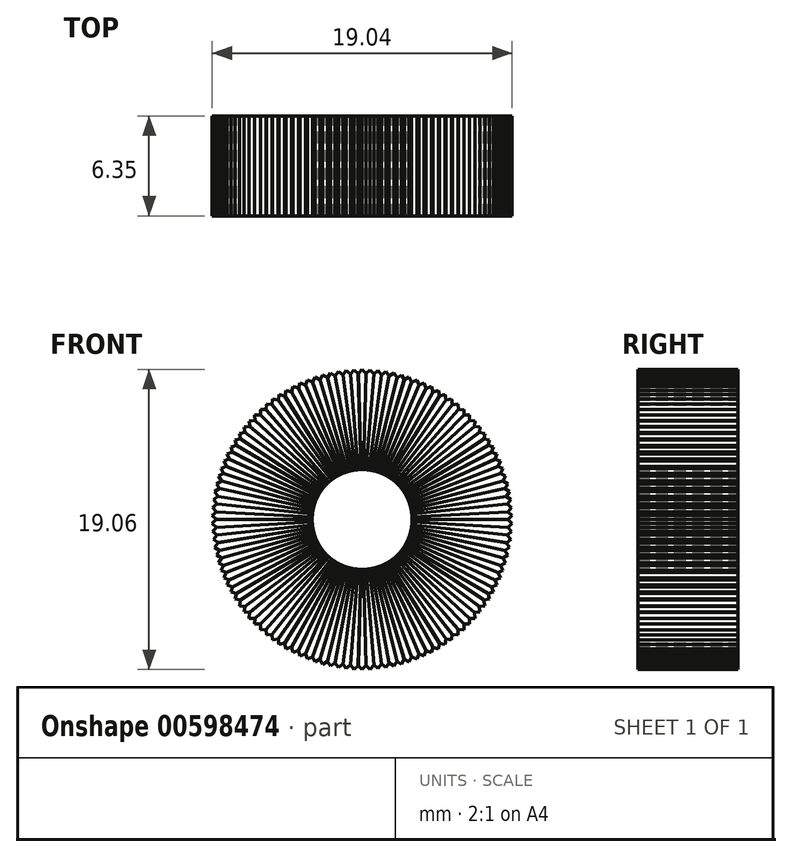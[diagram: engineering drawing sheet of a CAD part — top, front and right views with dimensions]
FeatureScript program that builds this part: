
annotation { "Feature Type Name" : "Feature", "Feature Type Description" : "" }
export const myFeature = defineFeature(function(context is Context, id is Id, definition is map)
    precondition{}
    {
        {
            var Q0;
            Q0=qCreatedBy(makeId("Front.planeOp"),FACE);
            var sketch = newSketch(context, id + "F0", { "sketchPlane" : qUnion([Q0])});
            skCircle(sketch, "E0", {"center": v(0, 0) * mm, "radius": 9.53 * mm});
            skCircle(sketch, "E1", {"center": v(0, 0) * mm, "radius": 3.18 * mm});
            skLineSegment(sketch, "E2", {"start": v(0, 0) * mm, "end": v(0, 9.53) * mm, "construction": true});
            skLineSegment(sketch, "E3.1.0", {"start": v(0, 0) * mm, "end": v(0.25, 9.52) * mm, "construction": true});
            skLineSegment(sketch, "E3.2.0", {"start": v(0, 0) * mm, "end": v(0.5, 9.51) * mm, "construction": true});
            skLineSegment(sketch, "E3.3.0", {"start": v(0, 0) * mm, "end": v(0.76, 9.5) * mm, "construction": true});
            skLineSegment(sketch, "E3.4.0", {"start": v(0, 0) * mm, "end": v(1.01, 9.47) * mm, "construction": true});
            skLineSegment(sketch, "E3.5.0", {"start": v(0, 0) * mm, "end": v(1.26, 9.44) * mm, "construction": true});
            skLineSegment(sketch, "E3.6.0", {"start": v(0, 0) * mm, "end": v(1.52, 9.4) * mm, "construction": true});
            skLineSegment(sketch, "E3.7.0", {"start": v(0, 0) * mm, "end": v(1.76, 9.36) * mm, "construction": true});
            skLineSegment(sketch, "E3.8.0", {"start": v(0, 0) * mm, "end": v(2.01, 9.3) * mm, "construction": true});
            skLineSegment(sketch, "E3.9.0", {"start": v(0, 0) * mm, "end": v(2.26, 9.25) * mm, "construction": true});
            skLineSegment(sketch, "E3.10.0", {"start": v(0, 0) * mm, "end": v(2.5, 9.19) * mm, "construction": true});
            skLineSegment(sketch, "E3.11.0", {"start": v(0, 0) * mm, "end": v(2.75, 9.12) * mm, "construction": true});
            skLineSegment(sketch, "E3.12.0", {"start": v(0, 0) * mm, "end": v(3, 9.04) * mm, "construction": true});
            skLineSegment(sketch, "E3.13.0", {"start": v(0, 0) * mm, "end": v(3.23, 8.96) * mm, "construction": true});
            skLineSegment(sketch, "E3.14.0", {"start": v(0, 0) * mm, "end": v(3.47, 8.87) * mm, "construction": true});
            skLineSegment(sketch, "E3.15.0", {"start": v(0, 0) * mm, "end": v(3.7, 8.78) * mm, "construction": true});
            skLineSegment(sketch, "E3.16.0", {"start": v(0, 0) * mm, "end": v(3.94, 8.67) * mm, "construction": true});
            skLineSegment(sketch, "E3.17.0", {"start": v(0, 0) * mm, "end": v(4.17, 8.57) * mm, "construction": true});
            skLineSegment(sketch, "E3.18.0", {"start": v(0, 0) * mm, "end": v(4.4, 8.45) * mm, "construction": true});
            skLineSegment(sketch, "E3.19.0", {"start": v(0, 0) * mm, "end": v(4.62, 8.33) * mm, "construction": true});
            skLineSegment(sketch, "E3.20.0", {"start": v(0, 0) * mm, "end": v(4.84, 8.2) * mm, "construction": true});
            skLineSegment(sketch, "E3.21.0", {"start": v(0, 0) * mm, "end": v(5.05, 8.07) * mm, "construction": true});
            skLineSegment(sketch, "E3.22.0", {"start": v(0, 0) * mm, "end": v(5.27, 7.94) * mm, "construction": true});
            skLineSegment(sketch, "E3.23.0", {"start": v(0, 0) * mm, "end": v(5.47, 7.8) * mm, "construction": true});
            skLineSegment(sketch, "E3.24.0", {"start": v(0, 0) * mm, "end": v(5.68, 7.65) * mm, "construction": true});
            skLineSegment(sketch, "E3.25.0", {"start": v(0, 0) * mm, "end": v(5.88, 7.5) * mm, "construction": true});
            skLineSegment(sketch, "E3.26.0", {"start": v(0, 0) * mm, "end": v(6.08, 7.33) * mm, "construction": true});
            skLineSegment(sketch, "E3.27.0", {"start": v(0, 0) * mm, "end": v(6.27, 7.17) * mm, "construction": true});
            skLineSegment(sketch, "E3.28.0", {"start": v(0, 0) * mm, "end": v(6.46, 7) * mm, "construction": true});
            skLineSegment(sketch, "E3.29.0", {"start": v(0, 0) * mm, "end": v(6.64, 6.82) * mm, "construction": true});
            skLineSegment(sketch, "E3.30.0", {"start": v(0, 0) * mm, "end": v(6.82, 6.64) * mm, "construction": true});
            skLineSegment(sketch, "E3.31.0", {"start": v(0, 0) * mm, "end": v(7, 6.46) * mm, "construction": true});
            skLineSegment(sketch, "E3.32.0", {"start": v(0, 0) * mm, "end": v(7.17, 6.27) * mm, "construction": true});
            skLineSegment(sketch, "E3.33.0", {"start": v(0, 0) * mm, "end": v(7.33, 6.08) * mm, "construction": true});
            skLineSegment(sketch, "E3.34.0", {"start": v(0, 0) * mm, "end": v(7.5, 5.88) * mm, "construction": true});
            skLineSegment(sketch, "E3.35.0", {"start": v(0, 0) * mm, "end": v(7.65, 5.68) * mm, "construction": true});
            skLineSegment(sketch, "E3.36.0", {"start": v(0, 0) * mm, "end": v(7.8, 5.47) * mm, "construction": true});
            skLineSegment(sketch, "E3.37.0", {"start": v(0, 0) * mm, "end": v(7.94, 5.27) * mm, "construction": true});
            skLineSegment(sketch, "E3.38.0", {"start": v(0, 0) * mm, "end": v(8.07, 5.05) * mm, "construction": true});
            skLineSegment(sketch, "E3.39.0", {"start": v(0, 0) * mm, "end": v(8.2, 4.84) * mm, "construction": true});
            skLineSegment(sketch, "E3.40.0", {"start": v(0, 0) * mm, "end": v(8.33, 4.62) * mm, "construction": true});
            skLineSegment(sketch, "E3.41.0", {"start": v(0, 0) * mm, "end": v(8.45, 4.4) * mm, "construction": true});
            skLineSegment(sketch, "E3.42.0", {"start": v(0, 0) * mm, "end": v(8.57, 4.17) * mm, "construction": true});
            skLineSegment(sketch, "E3.43.0", {"start": v(0, 0) * mm, "end": v(8.67, 3.94) * mm, "construction": true});
            skLineSegment(sketch, "E3.44.0", {"start": v(0, 0) * mm, "end": v(8.78, 3.7) * mm, "construction": true});
            skLineSegment(sketch, "E3.45.0", {"start": v(0, 0) * mm, "end": v(8.87, 3.47) * mm, "construction": true});
            skLineSegment(sketch, "E3.46.0", {"start": v(0, 0) * mm, "end": v(8.96, 3.23) * mm, "construction": true});
            skLineSegment(sketch, "E3.47.0", {"start": v(0, 0) * mm, "end": v(9.04, 3) * mm, "construction": true});
            skLineSegment(sketch, "E3.48.0", {"start": v(0, 0) * mm, "end": v(9.12, 2.75) * mm, "construction": true});
            skLineSegment(sketch, "E3.49.0", {"start": v(0, 0) * mm, "end": v(9.19, 2.5) * mm, "construction": true});
            skLineSegment(sketch, "E3.50.0", {"start": v(0, 0) * mm, "end": v(9.25, 2.26) * mm, "construction": true});
            skLineSegment(sketch, "E3.51.0", {"start": v(0, 0) * mm, "end": v(9.3, 2.01) * mm, "construction": true});
            skLineSegment(sketch, "E3.52.0", {"start": v(0, 0) * mm, "end": v(9.36, 1.76) * mm, "construction": true});
            skLineSegment(sketch, "E3.53.0", {"start": v(0, 0) * mm, "end": v(9.4, 1.52) * mm, "construction": true});
            skLineSegment(sketch, "E3.54.0", {"start": v(0, 0) * mm, "end": v(9.44, 1.26) * mm, "construction": true});
            skLineSegment(sketch, "E3.55.0", {"start": v(0, 0) * mm, "end": v(9.47, 1.01) * mm, "construction": true});
            skLineSegment(sketch, "E3.56.0", {"start": v(0, 0) * mm, "end": v(9.5, 0.76) * mm, "construction": true});
            skLineSegment(sketch, "E3.57.0", {"start": v(0, 0) * mm, "end": v(9.51, 0.5) * mm, "construction": true});
            skLineSegment(sketch, "E3.58.0", {"start": v(0, 0) * mm, "end": v(9.52, 0.25) * mm, "construction": true});
            skLineSegment(sketch, "E3.59.0", {"start": v(0, 0) * mm, "end": v(9.53, 0) * mm, "construction": true});
            skLineSegment(sketch, "E3.60.0", {"start": v(0, 0) * mm, "end": v(9.52, -0.25) * mm, "construction": true});
            skLineSegment(sketch, "E3.61.0", {"start": v(0, 0) * mm, "end": v(9.51, -0.5) * mm, "construction": true});
            skLineSegment(sketch, "E3.62.0", {"start": v(0, 0) * mm, "end": v(9.5, -0.76) * mm, "construction": true});
            skLineSegment(sketch, "E3.63.0", {"start": v(0, 0) * mm, "end": v(9.47, -1.01) * mm, "construction": true});
            skLineSegment(sketch, "E3.64.0", {"start": v(0, 0) * mm, "end": v(9.44, -1.26) * mm, "construction": true});
            skLineSegment(sketch, "E3.65.0", {"start": v(0, 0) * mm, "end": v(9.4, -1.52) * mm, "construction": true});
            skLineSegment(sketch, "E3.66.0", {"start": v(0, 0) * mm, "end": v(9.36, -1.76) * mm, "construction": true});
            skLineSegment(sketch, "E3.67.0", {"start": v(0, 0) * mm, "end": v(9.3, -2.01) * mm, "construction": true});
            skLineSegment(sketch, "E3.68.0", {"start": v(0, 0) * mm, "end": v(9.25, -2.26) * mm, "construction": true});
            skLineSegment(sketch, "E3.69.0", {"start": v(0, 0) * mm, "end": v(9.19, -2.5) * mm, "construction": true});
            skLineSegment(sketch, "E3.70.0", {"start": v(0, 0) * mm, "end": v(9.12, -2.75) * mm, "construction": true});
            skLineSegment(sketch, "E3.71.0", {"start": v(0, 0) * mm, "end": v(9.04, -3) * mm, "construction": true});
            skLineSegment(sketch, "E3.72.0", {"start": v(0, 0) * mm, "end": v(8.96, -3.23) * mm, "construction": true});
            skLineSegment(sketch, "E3.73.0", {"start": v(0, 0) * mm, "end": v(8.87, -3.47) * mm, "construction": true});
            skLineSegment(sketch, "E3.74.0", {"start": v(0, 0) * mm, "end": v(8.78, -3.7) * mm, "construction": true});
            skLineSegment(sketch, "E3.75.0", {"start": v(0, 0) * mm, "end": v(8.67, -3.94) * mm, "construction": true});
            skLineSegment(sketch, "E3.76.0", {"start": v(0, 0) * mm, "end": v(8.57, -4.17) * mm, "construction": true});
            skLineSegment(sketch, "E3.77.0", {"start": v(0, 0) * mm, "end": v(8.45, -4.4) * mm, "construction": true});
            skLineSegment(sketch, "E3.78.0", {"start": v(0, 0) * mm, "end": v(8.33, -4.62) * mm, "construction": true});
            skLineSegment(sketch, "E3.79.0", {"start": v(0, 0) * mm, "end": v(8.2, -4.84) * mm, "construction": true});
            skLineSegment(sketch, "E3.80.0", {"start": v(0, 0) * mm, "end": v(8.07, -5.05) * mm, "construction": true});
            skLineSegment(sketch, "E3.81.0", {"start": v(0, 0) * mm, "end": v(7.94, -5.27) * mm, "construction": true});
            skLineSegment(sketch, "E3.82.0", {"start": v(0, 0) * mm, "end": v(7.8, -5.47) * mm, "construction": true});
            skLineSegment(sketch, "E3.83.0", {"start": v(0, 0) * mm, "end": v(7.65, -5.68) * mm, "construction": true});
            skLineSegment(sketch, "E3.84.0", {"start": v(0, 0) * mm, "end": v(7.5, -5.88) * mm, "construction": true});
            skLineSegment(sketch, "E3.85.0", {"start": v(0, 0) * mm, "end": v(7.33, -6.08) * mm, "construction": true});
            skLineSegment(sketch, "E3.86.0", {"start": v(0, 0) * mm, "end": v(7.17, -6.27) * mm, "construction": true});
            skLineSegment(sketch, "E3.87.0", {"start": v(0, 0) * mm, "end": v(7, -6.46) * mm, "construction": true});
            skLineSegment(sketch, "E3.88.0", {"start": v(0, 0) * mm, "end": v(6.82, -6.64) * mm, "construction": true});
            skLineSegment(sketch, "E3.89.0", {"start": v(0, 0) * mm, "end": v(6.64, -6.82) * mm, "construction": true});
            skLineSegment(sketch, "E3.90.0", {"start": v(0, 0) * mm, "end": v(6.46, -7) * mm, "construction": true});
            skLineSegment(sketch, "E3.91.0", {"start": v(0, 0) * mm, "end": v(6.27, -7.17) * mm, "construction": true});
            skLineSegment(sketch, "E3.92.0", {"start": v(0, 0) * mm, "end": v(6.08, -7.33) * mm, "construction": true});
            skLineSegment(sketch, "E3.93.0", {"start": v(0, 0) * mm, "end": v(5.88, -7.5) * mm, "construction": true});
            skLineSegment(sketch, "E3.94.0", {"start": v(0, 0) * mm, "end": v(5.68, -7.65) * mm, "construction": true});
            skLineSegment(sketch, "E3.95.0", {"start": v(0, 0) * mm, "end": v(5.47, -7.8) * mm, "construction": true});
            skLineSegment(sketch, "E3.96.0", {"start": v(0, 0) * mm, "end": v(5.27, -7.94) * mm, "construction": true});
            skLineSegment(sketch, "E3.97.0", {"start": v(0, 0) * mm, "end": v(5.05, -8.07) * mm, "construction": true});
            skLineSegment(sketch, "E3.98.0", {"start": v(0, 0) * mm, "end": v(4.84, -8.2) * mm, "construction": true});
            skLineSegment(sketch, "E3.99.0", {"start": v(0, 0) * mm, "end": v(4.62, -8.33) * mm, "construction": true});
            skLineSegment(sketch, "E3.100.0", {"start": v(0, 0) * mm, "end": v(4.4, -8.45) * mm, "construction": true});
            skLineSegment(sketch, "E3.101.0", {"start": v(0, 0) * mm, "end": v(4.17, -8.57) * mm, "construction": true});
            skLineSegment(sketch, "E3.102.0", {"start": v(0, 0) * mm, "end": v(3.94, -8.67) * mm, "construction": true});
            skLineSegment(sketch, "E3.103.0", {"start": v(0, 0) * mm, "end": v(3.7, -8.78) * mm, "construction": true});
            skLineSegment(sketch, "E3.104.0", {"start": v(0, 0) * mm, "end": v(3.47, -8.87) * mm, "construction": true});
            skLineSegment(sketch, "E3.105.0", {"start": v(0, 0) * mm, "end": v(3.23, -8.96) * mm, "construction": true});
            skLineSegment(sketch, "E3.106.0", {"start": v(0, 0) * mm, "end": v(3, -9.04) * mm, "construction": true});
            skLineSegment(sketch, "E3.107.0", {"start": v(0, 0) * mm, "end": v(2.75, -9.12) * mm, "construction": true});
            skLineSegment(sketch, "E3.108.0", {"start": v(0, 0) * mm, "end": v(2.5, -9.19) * mm, "construction": true});
            skLineSegment(sketch, "E3.109.0", {"start": v(0, 0) * mm, "end": v(2.26, -9.25) * mm, "construction": true});
            skLineSegment(sketch, "E3.110.0", {"start": v(0, 0) * mm, "end": v(2.01, -9.3) * mm, "construction": true});
            skLineSegment(sketch, "E3.111.0", {"start": v(0, 0) * mm, "end": v(1.76, -9.36) * mm, "construction": true});
            skLineSegment(sketch, "E3.112.0", {"start": v(0, 0) * mm, "end": v(1.52, -9.4) * mm, "construction": true});
            skLineSegment(sketch, "E3.113.0", {"start": v(0, 0) * mm, "end": v(1.26, -9.44) * mm, "construction": true});
            skLineSegment(sketch, "E3.114.0", {"start": v(0, 0) * mm, "end": v(1.01, -9.47) * mm, "construction": true});
            skLineSegment(sketch, "E3.115.0", {"start": v(0, 0) * mm, "end": v(0.76, -9.5) * mm, "construction": true});
            skLineSegment(sketch, "E3.116.0", {"start": v(0, 0) * mm, "end": v(0.5, -9.51) * mm, "construction": true});
            skLineSegment(sketch, "E3.117.0", {"start": v(0, 0) * mm, "end": v(0.25, -9.52) * mm, "construction": true});
            skLineSegment(sketch, "E3.anchor2", {"start": v(0, 0) * mm, "end": v(-0.25, 9.52) * mm, "construction": true});
            skLineSegment(sketch, "E4.2.118.0", {"start": v(0, 0) * mm, "end": v(0, -9.53) * mm, "construction": true});
            skLineSegment(sketch, "E4.2.119.0", {"start": v(0, 0) * mm, "end": v(-0.25, -9.52) * mm, "construction": true});
            skLineSegment(sketch, "E4.2.120.0", {"start": v(0, 0) * mm, "end": v(-0.5, -9.51) * mm, "construction": true});
            skLineSegment(sketch, "E4.2.121.0", {"start": v(0, 0) * mm, "end": v(-0.76, -9.5) * mm, "construction": true});
            skLineSegment(sketch, "E4.2.122.0", {"start": v(0, 0) * mm, "end": v(-1.01, -9.47) * mm, "construction": true});
            skLineSegment(sketch, "E4.2.123.0", {"start": v(0, 0) * mm, "end": v(-1.26, -9.44) * mm, "construction": true});
            skLineSegment(sketch, "E4.2.124.0", {"start": v(0, 0) * mm, "end": v(-1.52, -9.4) * mm, "construction": true});
            skLineSegment(sketch, "E4.2.125.0", {"start": v(0, 0) * mm, "end": v(-1.76, -9.36) * mm, "construction": true});
            skLineSegment(sketch, "E4.2.126.0", {"start": v(0, 0) * mm, "end": v(-2.01, -9.3) * mm, "construction": true});
            skLineSegment(sketch, "E4.2.127.0", {"start": v(0, 0) * mm, "end": v(-2.26, -9.25) * mm, "construction": true});
            skLineSegment(sketch, "E4.2.128.0", {"start": v(0, 0) * mm, "end": v(-2.5, -9.19) * mm, "construction": true});
            skLineSegment(sketch, "E4.2.129.0", {"start": v(0, 0) * mm, "end": v(-2.75, -9.12) * mm, "construction": true});
            skLineSegment(sketch, "E4.2.130.0", {"start": v(0, 0) * mm, "end": v(-3, -9.04) * mm, "construction": true});
            skLineSegment(sketch, "E4.2.131.0", {"start": v(0, 0) * mm, "end": v(-3.23, -8.96) * mm, "construction": true});
            skLineSegment(sketch, "E4.2.132.0", {"start": v(0, 0) * mm, "end": v(-3.47, -8.87) * mm, "construction": true});
            skLineSegment(sketch, "E4.2.133.0", {"start": v(0, 0) * mm, "end": v(-3.7, -8.78) * mm, "construction": true});
            skLineSegment(sketch, "E4.2.134.0", {"start": v(0, 0) * mm, "end": v(-3.94, -8.67) * mm, "construction": true});
            skLineSegment(sketch, "E4.2.135.0", {"start": v(0, 0) * mm, "end": v(-4.17, -8.57) * mm, "construction": true});
            skLineSegment(sketch, "E4.2.136.0", {"start": v(0, 0) * mm, "end": v(-4.4, -8.45) * mm, "construction": true});
            skLineSegment(sketch, "E4.2.137.0", {"start": v(0, 0) * mm, "end": v(-4.62, -8.33) * mm, "construction": true});
            skLineSegment(sketch, "E4.2.138.0", {"start": v(0, 0) * mm, "end": v(-4.84, -8.2) * mm, "construction": true});
            skLineSegment(sketch, "E4.2.139.0", {"start": v(0, 0) * mm, "end": v(-5.05, -8.07) * mm, "construction": true});
            skLineSegment(sketch, "E4.2.140.0", {"start": v(0, 0) * mm, "end": v(-5.27, -7.94) * mm, "construction": true});
            skLineSegment(sketch, "E4.2.141.0", {"start": v(0, 0) * mm, "end": v(-5.47, -7.8) * mm, "construction": true});
            skLineSegment(sketch, "E4.2.142.0", {"start": v(0, 0) * mm, "end": v(-5.68, -7.65) * mm, "construction": true});
            skLineSegment(sketch, "E4.2.143.0", {"start": v(0, 0) * mm, "end": v(-5.88, -7.5) * mm, "construction": true});
            skLineSegment(sketch, "E4.2.144.0", {"start": v(0, 0) * mm, "end": v(-6.08, -7.33) * mm, "construction": true});
            skLineSegment(sketch, "E4.2.145.0", {"start": v(0, 0) * mm, "end": v(-6.27, -7.17) * mm, "construction": true});
            skLineSegment(sketch, "E4.2.146.0", {"start": v(0, 0) * mm, "end": v(-6.46, -7) * mm, "construction": true});
            skLineSegment(sketch, "E4.2.147.0", {"start": v(0, 0) * mm, "end": v(-6.64, -6.82) * mm, "construction": true});
            skLineSegment(sketch, "E4.2.148.0", {"start": v(0, 0) * mm, "end": v(-6.82, -6.64) * mm, "construction": true});
            skLineSegment(sketch, "E4.2.149.0", {"start": v(0, 0) * mm, "end": v(-7, -6.46) * mm, "construction": true});
            skLineSegment(sketch, "E4.2.150.0", {"start": v(0, 0) * mm, "end": v(-7.17, -6.27) * mm, "construction": true});
            skLineSegment(sketch, "E4.2.151.0", {"start": v(0, 0) * mm, "end": v(-7.33, -6.08) * mm, "construction": true});
            skLineSegment(sketch, "E4.2.152.0", {"start": v(0, 0) * mm, "end": v(-7.5, -5.88) * mm, "construction": true});
            skLineSegment(sketch, "E4.2.153.0", {"start": v(0, 0) * mm, "end": v(-7.65, -5.68) * mm, "construction": true});
            skLineSegment(sketch, "E4.2.154.0", {"start": v(0, 0) * mm, "end": v(-7.8, -5.47) * mm, "construction": true});
            skLineSegment(sketch, "E4.2.155.0", {"start": v(0, 0) * mm, "end": v(-7.94, -5.27) * mm, "construction": true});
            skLineSegment(sketch, "E4.2.156.0", {"start": v(0, 0) * mm, "end": v(-8.07, -5.05) * mm, "construction": true});
            skLineSegment(sketch, "E4.2.157.0", {"start": v(0, 0) * mm, "end": v(-8.2, -4.84) * mm, "construction": true});
            skLineSegment(sketch, "E4.2.158.0", {"start": v(0, 0) * mm, "end": v(-8.33, -4.62) * mm, "construction": true});
            skLineSegment(sketch, "E4.2.159.0", {"start": v(0, 0) * mm, "end": v(-8.45, -4.4) * mm, "construction": true});
            skLineSegment(sketch, "E4.2.160.0", {"start": v(0, 0) * mm, "end": v(-8.57, -4.17) * mm, "construction": true});
            skLineSegment(sketch, "E4.2.161.0", {"start": v(0, 0) * mm, "end": v(-8.67, -3.94) * mm, "construction": true});
            skLineSegment(sketch, "E4.2.162.0", {"start": v(0, 0) * mm, "end": v(-8.78, -3.7) * mm, "construction": true});
            skLineSegment(sketch, "E4.2.163.0", {"start": v(0, 0) * mm, "end": v(-8.87, -3.47) * mm, "construction": true});
            skLineSegment(sketch, "E4.2.164.0", {"start": v(0, 0) * mm, "end": v(-8.96, -3.23) * mm, "construction": true});
            skLineSegment(sketch, "E4.2.165.0", {"start": v(0, 0) * mm, "end": v(-9.04, -3) * mm, "construction": true});
            skLineSegment(sketch, "E4.2.166.0", {"start": v(0, 0) * mm, "end": v(-9.12, -2.75) * mm, "construction": true});
            skLineSegment(sketch, "E4.2.167.0", {"start": v(0, 0) * mm, "end": v(-9.19, -2.5) * mm, "construction": true});
            skLineSegment(sketch, "E4.2.168.0", {"start": v(0, 0) * mm, "end": v(-9.25, -2.26) * mm, "construction": true});
            skLineSegment(sketch, "E4.2.169.0", {"start": v(0, 0) * mm, "end": v(-9.3, -2.01) * mm, "construction": true});
            skLineSegment(sketch, "E4.2.170.0", {"start": v(0, 0) * mm, "end": v(-9.36, -1.76) * mm, "construction": true});
            skLineSegment(sketch, "E4.2.171.0", {"start": v(0, 0) * mm, "end": v(-9.4, -1.52) * mm, "construction": true});
            skLineSegment(sketch, "E4.2.172.0", {"start": v(0, 0) * mm, "end": v(-9.44, -1.26) * mm, "construction": true});
            skLineSegment(sketch, "E4.2.173.0", {"start": v(0, 0) * mm, "end": v(-9.47, -1.01) * mm, "construction": true});
            skLineSegment(sketch, "E4.2.174.0", {"start": v(0, 0) * mm, "end": v(-9.5, -0.76) * mm, "construction": true});
            skLineSegment(sketch, "E4.2.175.0", {"start": v(0, 0) * mm, "end": v(-9.51, -0.5) * mm, "construction": true});
            skLineSegment(sketch, "E4.2.176.0", {"start": v(0, 0) * mm, "end": v(-9.52, -0.25) * mm, "construction": true});
            skLineSegment(sketch, "E4.2.177.0", {"start": v(0, 0) * mm, "end": v(-9.52, 0) * mm, "construction": true});
            skLineSegment(sketch, "E4.2.178.0", {"start": v(0, 0) * mm, "end": v(-9.52, 0.25) * mm, "construction": true});
            skLineSegment(sketch, "E4.2.179.0", {"start": v(0, 0) * mm, "end": v(-9.51, 0.5) * mm, "construction": true});
            skLineSegment(sketch, "E4.2.180.0", {"start": v(0, 0) * mm, "end": v(-9.5, 0.76) * mm, "construction": true});
            skLineSegment(sketch, "E4.2.181.0", {"start": v(0, 0) * mm, "end": v(-9.47, 1.01) * mm, "construction": true});
            skLineSegment(sketch, "E4.2.182.0", {"start": v(0, 0) * mm, "end": v(-9.44, 1.26) * mm, "construction": true});
            skLineSegment(sketch, "E4.2.183.0", {"start": v(0, 0) * mm, "end": v(-9.4, 1.52) * mm, "construction": true});
            skLineSegment(sketch, "E4.2.184.0", {"start": v(0, 0) * mm, "end": v(-9.36, 1.76) * mm, "construction": true});
            skLineSegment(sketch, "E4.2.185.0", {"start": v(0, 0) * mm, "end": v(-9.3, 2.01) * mm, "construction": true});
            skLineSegment(sketch, "E4.2.186.0", {"start": v(0, 0) * mm, "end": v(-9.25, 2.26) * mm, "construction": true});
            skLineSegment(sketch, "E4.2.187.0", {"start": v(0, 0) * mm, "end": v(-9.19, 2.5) * mm, "construction": true});
            skLineSegment(sketch, "E4.2.188.0", {"start": v(0, 0) * mm, "end": v(-9.12, 2.75) * mm, "construction": true});
            skLineSegment(sketch, "E4.2.189.0", {"start": v(0, 0) * mm, "end": v(-9.04, 3) * mm, "construction": true});
            skLineSegment(sketch, "E4.2.190.0", {"start": v(0, 0) * mm, "end": v(-8.96, 3.23) * mm, "construction": true});
            skLineSegment(sketch, "E4.2.191.0", {"start": v(0, 0) * mm, "end": v(-8.87, 3.47) * mm, "construction": true});
            skLineSegment(sketch, "E4.2.192.0", {"start": v(0, 0) * mm, "end": v(-8.78, 3.7) * mm, "construction": true});
            skLineSegment(sketch, "E4.2.193.0", {"start": v(0, 0) * mm, "end": v(-8.67, 3.94) * mm, "construction": true});
            skLineSegment(sketch, "E4.2.194.0", {"start": v(0, 0) * mm, "end": v(-8.57, 4.17) * mm, "construction": true});
            skLineSegment(sketch, "E4.2.195.0", {"start": v(0, 0) * mm, "end": v(-8.45, 4.4) * mm, "construction": true});
            skLineSegment(sketch, "E4.2.196.0", {"start": v(0, 0) * mm, "end": v(-8.33, 4.62) * mm, "construction": true});
            skLineSegment(sketch, "E4.2.197.0", {"start": v(0, 0) * mm, "end": v(-8.2, 4.84) * mm, "construction": true});
            skLineSegment(sketch, "E4.2.198.0", {"start": v(0, 0) * mm, "end": v(-8.07, 5.05) * mm, "construction": true});
            skLineSegment(sketch, "E4.2.199.0", {"start": v(0, 0) * mm, "end": v(-7.94, 5.27) * mm, "construction": true});
            skLineSegment(sketch, "E4.2.200.0", {"start": v(0, 0) * mm, "end": v(-7.8, 5.47) * mm, "construction": true});
            skLineSegment(sketch, "E4.2.201.0", {"start": v(0, 0) * mm, "end": v(-7.65, 5.68) * mm, "construction": true});
            skLineSegment(sketch, "E4.2.202.0", {"start": v(0, 0) * mm, "end": v(-7.5, 5.88) * mm, "construction": true});
            skLineSegment(sketch, "E4.2.203.0", {"start": v(0, 0) * mm, "end": v(-7.33, 6.08) * mm, "construction": true});
            skLineSegment(sketch, "E4.2.204.0", {"start": v(0, 0) * mm, "end": v(-7.17, 6.27) * mm, "construction": true});
            skLineSegment(sketch, "E4.2.205.0", {"start": v(0, 0) * mm, "end": v(-7, 6.46) * mm, "construction": true});
            skLineSegment(sketch, "E4.2.206.0", {"start": v(0, 0) * mm, "end": v(-6.82, 6.64) * mm, "construction": true});
            skLineSegment(sketch, "E4.2.207.0", {"start": v(0, 0) * mm, "end": v(-6.64, 6.82) * mm, "construction": true});
            skLineSegment(sketch, "E4.2.208.0", {"start": v(0, 0) * mm, "end": v(-6.46, 7) * mm, "construction": true});
            skLineSegment(sketch, "E4.2.209.0", {"start": v(0, 0) * mm, "end": v(-6.27, 7.17) * mm, "construction": true});
            skLineSegment(sketch, "E4.2.210.0", {"start": v(0, 0) * mm, "end": v(-6.08, 7.33) * mm, "construction": true});
            skLineSegment(sketch, "E4.2.211.0", {"start": v(0, 0) * mm, "end": v(-5.88, 7.5) * mm, "construction": true});
            skLineSegment(sketch, "E4.2.212.0", {"start": v(0, 0) * mm, "end": v(-5.68, 7.65) * mm, "construction": true});
            skLineSegment(sketch, "E4.2.213.0", {"start": v(0, 0) * mm, "end": v(-5.47, 7.8) * mm, "construction": true});
            skLineSegment(sketch, "E4.2.214.0", {"start": v(0, 0) * mm, "end": v(-5.27, 7.94) * mm, "construction": true});
            skLineSegment(sketch, "E4.2.215.0", {"start": v(0, 0) * mm, "end": v(-5.05, 8.07) * mm, "construction": true});
            skLineSegment(sketch, "E4.2.216.0", {"start": v(0, 0) * mm, "end": v(-4.84, 8.2) * mm, "construction": true});
            skLineSegment(sketch, "E4.2.217.0", {"start": v(0, 0) * mm, "end": v(-4.62, 8.33) * mm, "construction": true});
            skLineSegment(sketch, "E4.2.218.0", {"start": v(0, 0) * mm, "end": v(-4.4, 8.45) * mm, "construction": true});
            skLineSegment(sketch, "E4.2.219.0", {"start": v(0, 0) * mm, "end": v(-4.17, 8.57) * mm, "construction": true});
            skLineSegment(sketch, "E4.2.220.0", {"start": v(0, 0) * mm, "end": v(-3.94, 8.67) * mm, "construction": true});
            skLineSegment(sketch, "E4.2.221.0", {"start": v(0, 0) * mm, "end": v(-3.7, 8.78) * mm, "construction": true});
            skLineSegment(sketch, "E4.2.222.0", {"start": v(0, 0) * mm, "end": v(-3.47, 8.87) * mm, "construction": true});
            skLineSegment(sketch, "E4.2.223.0", {"start": v(0, 0) * mm, "end": v(-3.23, 8.96) * mm, "construction": true});
            skLineSegment(sketch, "E4.2.224.0", {"start": v(0, 0) * mm, "end": v(-3, 9.04) * mm, "construction": true});
            skLineSegment(sketch, "E4.2.225.0", {"start": v(0, 0) * mm, "end": v(-2.75, 9.12) * mm, "construction": true});
            skLineSegment(sketch, "E4.2.226.0", {"start": v(0, 0) * mm, "end": v(-2.5, 9.19) * mm, "construction": true});
            skLineSegment(sketch, "E4.2.227.0", {"start": v(0, 0) * mm, "end": v(-2.26, 9.25) * mm, "construction": true});
            skLineSegment(sketch, "E4.2.228.0", {"start": v(0, 0) * mm, "end": v(-2.01, 9.3) * mm, "construction": true});
            skLineSegment(sketch, "E4.2.229.0", {"start": v(0, 0) * mm, "end": v(-1.76, 9.36) * mm, "construction": true});
            skLineSegment(sketch, "E4.2.230.0", {"start": v(0, 0) * mm, "end": v(-1.52, 9.4) * mm, "construction": true});
            skLineSegment(sketch, "E4.2.231.0", {"start": v(0, 0) * mm, "end": v(-1.26, 9.44) * mm, "construction": true});
            skLineSegment(sketch, "E4.2.232.0", {"start": v(0, 0) * mm, "end": v(-1.01, 9.47) * mm, "construction": true});
            skLineSegment(sketch, "E4.2.233.0", {"start": v(0, 0) * mm, "end": v(-0.76, 9.5) * mm, "construction": true});
            skLineSegment(sketch, "E4.2.234.0", {"start": v(0, 0) * mm, "end": v(-0.5, 9.51) * mm, "construction": true});
            skCircle(sketch, "E5", {"center": v(0, 0) * mm, "radius": 9.27 * mm});
            skLineSegment(sketch, "E6", {"start": v(-0.25, 9.52) * mm, "end": v(0, 0) * mm});
            skLineSegment(sketch, "E7", {"start": v(0.25, 9.52) * mm, "end": v(0, 0) * mm});
            skLineSegment(sketch, "E8", {"start": v(0, 9.53) * mm, "end": v(-0.25, 9.26) * mm});
            skLineSegment(sketch, "E9", {"start": v(0, 9.53) * mm, "end": v(0.25, 9.27) * mm});
            skSolve(sketch);
        }
        {
            var Q0;
            {var subQ0=sQuery(id+"F0.wireOp",EDGE,"E9");Q0=makeQuery(id+"F0.imprint","IMPRINT",FACE,{"disambiguationData":[TD([[makeQuery(id+"F0.imprint","IMPRINT",EDGE,{"derivedFrom":subQ0}),-1.0]])]});}
            var Q1;
            {var subQ1=sQuery(id+"F0.wireOp",EDGE,"E6");var subQ3=sQuery(id+"F0.wireOp",EDGE,"E1");var subQ4=makeQuery(id+"F0.imprint","INTERSECT",VERTEX,{"derivedFrom":[subQ3,subQ1]});Q1=makeQuery(id+"F0.imprint","IMPRINT",FACE,{"disambiguationData":[TD([[makeQuery(id+"F0.imprint","IMPRINT",EDGE,{"disambiguationData":[TD([[subQ4,1.0]])],"derivedFrom":subQ3}),-1.0]])]});}
            extrude(context, id + "F1", {"entities" : qUnion([Q0, Q1]), "depth" : 6.35 * mm, "offsetDistance" : 25.4 * mm});
        }
        {
            var Q0;
            Q0=qCreatedBy(makeId("Top.planeOp"),FACE);
            var sketch = newSketch(context, id + "F2", { "sketchPlane" : qUnion([Q0])});
            skLineSegment(sketch, "E10", {"start": v(0, 0.27) * mm, "end": v(0, -6.08) * mm});
            skSolve(sketch);
        }
        {
            var Q0;
            Q0=makeQuery(id+"F1.opExtrude","SWEPT_BODY",BODY,{"disambiguationData":[OSD([sQuery(id+"F0.wireOp",EDGE,"E1"),sQuery(id+"F0.wireOp",EDGE,"E6"),sQuery(id+"F0.wireOp",EDGE,"E7"),sQuery(id+"F0.wireOp",EDGE,"E8"),sQuery(id+"F0.wireOp",EDGE,"E9")])]});
            var Q1;
            Q1=sQuery(id+"F2.wireOp",EDGE,"E10");
            circularPattern(context, id + "F3", {"entities" : qUnion([Q0]), "axis" : qUnion([Q1]), "angle" : 360 * degree, "instanceCount" : 118, "equalSpace" : true, "computeTransformsWithoutBuiltin" : true});
        }
    });
